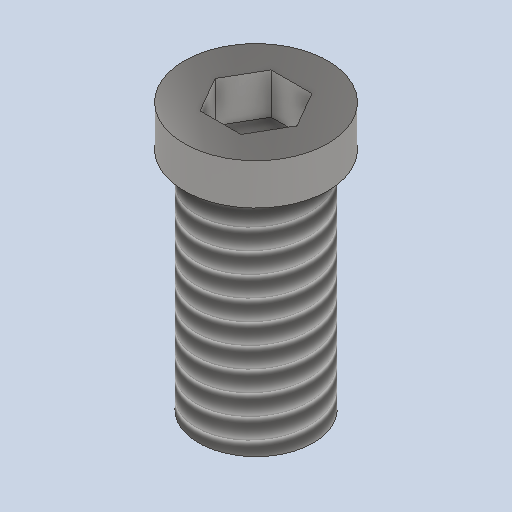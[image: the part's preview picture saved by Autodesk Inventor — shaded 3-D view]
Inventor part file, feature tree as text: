
AUTODESK INVENTOR PART (.ipt)
format: ipt  version: 2022 (Build 260153000, 153)  size: 170,496 bytes
history: native  units: in
note: dims shown in document units (in); Inventor stores cm internally (conversion verified against a paired STEP export)
features: extrude x2, sketch x2, thread x1
ambient origin geometry x8: Origin, YZ Plane, XZ Plane, XY Plane, X Axis, Y Axis, Z Axis, Center Point
bodies: Solid1 (feature_tree)
feature tree (5):
  extrude  "Extrusion1"  Depth=0.2165in TaperAngle=0.0deg
  extrude  "Extrusion2"  Depth=0.0394in
  thread  "Thread1"  [1 undecoded]
  sketch  "Sketch1"  dims[d0=0.1102in d1=0.2165in d2=0.0in]
  sketch  "Sketch2"  dims[d3=0.1378in d4=0.0394in d5=0.0394in d6=0.0in d7=0.2362in d8=0.0in]
note: 1 required parameter value undecoded (feature->parameter linkage not recoverable at this tier; creation-order binding heuristic only, values carry confidence <= 0.55)
